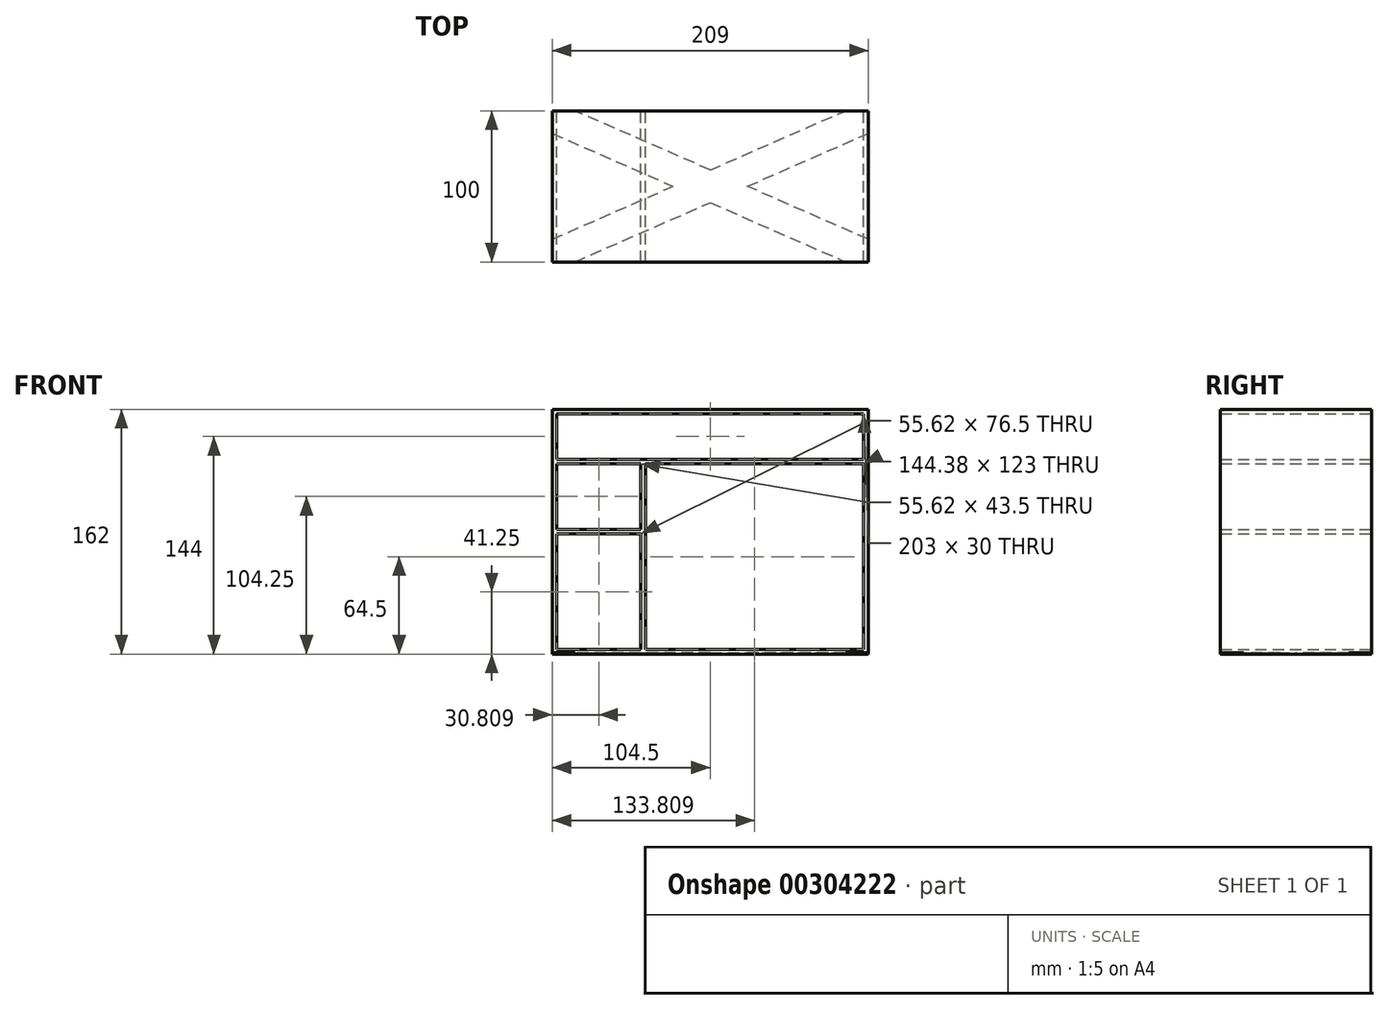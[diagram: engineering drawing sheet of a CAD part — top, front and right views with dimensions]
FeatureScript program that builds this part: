
annotation { "Feature Type Name" : "Feature", "Feature Type Description" : "" }
export const myFeature = defineFeature(function(context is Context, id is Id, definition is map)
    precondition{}
    {
        {
            var Q0;
            Q0=qCreatedBy(makeId("Front.planeOp"),FACE);
            var sketch = newSketch(context, id + "F0", { "sketchPlane" : qUnion([Q0])});
            skLineSegment(sketch, "E0.bottom", {"start": v(0, 0) * mm, "end": v(209, 0) * mm});
            skLineSegment(sketch, "E0.top", {"start": v(0, 162) * mm, "end": v(209, 162) * mm});
            skLineSegment(sketch, "E0.left", {"start": v(0, 0) * mm, "end": v(0, 162) * mm});
            skLineSegment(sketch, "E0.right", {"start": v(209, 0) * mm, "end": v(209, 162) * mm});
            skLineSegment(sketch, "E1", {"start": v(3, 159) * mm, "end": v(206, 159) * mm});
            skLineSegment(sketch, "E2", {"start": v(206, 159) * mm, "end": v(206, 129) * mm});
            skLineSegment(sketch, "E3", {"start": v(206, 3) * mm, "end": v(106, 3) * mm});
            skLineSegment(sketch, "E4", {"start": v(3, 159) * mm, "end": v(3, 129) * mm});
            skLineSegment(sketch, "E5", {"start": v(3, 129) * mm, "end": v(206, 129) * mm});
            skLineSegment(sketch, "E6", {"start": v(3, 126) * mm, "end": v(103, 126) * mm});
            skPoint(sketch, "E7.end.orphan", {"position": v(104.5, 3) * mm});
            skLineSegment(sketch, "E8", {"start": v(3, 79.5) * mm, "end": v(58.62, 79.5) * mm});
            skLineSegment(sketch, "E9", {"start": v(3, 82.5) * mm, "end": v(58.62, 82.5) * mm});
            skPoint(sketch, "E10.start.orphan", {"position": v(3, 81) * mm});
            skLineSegment(sketch, "E11.trimOffspring", {"start": v(103, 3) * mm, "end": v(3, 3) * mm});
            skLineSegment(sketch, "E12.trimOffspring", {"start": v(106, 126) * mm, "end": v(206, 126) * mm});
            skPoint(sketch, "E13.orphan", {"position": v(104.5, 126) * mm});
            skLineSegment(sketch, "E14.trimOffspring", {"start": v(206, 126) * mm, "end": v(206, 3) * mm});
            skLineSegment(sketch, "E15.trimOffspring", {"start": v(3, 126) * mm, "end": v(3, 82.5) * mm});
            skLineSegment(sketch, "E16.trimOffspring", {"start": v(3, 79.5) * mm, "end": v(3, 3) * mm});
            skLineSegment(sketch, "E17.left", {"start": v(0, 162) * mm, "end": v(0, 0) * mm});
            skLineSegment(sketch, "E17.right", {"start": v(209, 162) * mm, "end": v(209, 0) * mm});
            skLineSegment(sketch, "E18", {"start": v(58.62, 126) * mm, "end": v(58.62, 82.5) * mm});
            skLineSegment(sketch, "E19", {"start": v(61.62, 126) * mm, "end": v(61.62, 3) * mm});
            skLineSegment(sketch, "E20", {"start": v(58.62, 126) * mm, "end": v(60.12, 126) * mm, "construction": true});
            skLineSegment(sketch, "E21", {"start": v(60.12, 126) * mm, "end": v(61.62, 126) * mm, "construction": true});
            skLineSegment(sketch, "E22.trimOffspring", {"start": v(58.62, 79.5) * mm, "end": v(58.62, 3) * mm});
            skLineSegment(sketch, "E23", {"start": v(103, 126) * mm, "end": v(106, 126) * mm});
            skLineSegment(sketch, "E24", {"start": v(103, 3) * mm, "end": v(106, 3) * mm});
            skSolve(sketch);
        }
        {
            var Q0;
            Q0=makeQuery(id+"F0.imprint","IMPRINT",FACE,{"disambiguationData":[TD([[makeQuery(id+"F0.imprint","IMPRINT",EDGE,{"derivedFrom":sQuery(id+"F0.wireOp",EDGE,"E1")}),1.0]])]});
            extrude(context, id + "F1", {"entities" : qUnion([Q0]), "depth" : 100 * mm});
        }
        {
            var Q0;
            Q0=makeQuery(id+"F1.opExtrude","SWEPT_FACE",FACE,{"disambiguationData":[OSD([sQuery(id+"F0.wireOp",EDGE,"E0.bottom")])]});
            var sketch = newSketch(context, id + "F2", { "sketchPlane" : qUnion([Q0])});
            skLineSegment(sketch, "E25", {"start": v(15, 100) * mm, "end": v(104.5, 60.79) * mm});
            skLineSegment(sketch, "E26", {"start": v(0, 85) * mm, "end": v(79.88, 50) * mm});
            skLineSegment(sketch, "E27", {"start": v(0, 100) * mm, "end": v(15, 100) * mm, "construction": true});
            skLineSegment(sketch, "E28", {"start": v(0, 100) * mm, "end": v(0, 85) * mm, "construction": true});
            skLineSegment(sketch, "E29", {"start": v(209, 15) * mm, "end": v(209, 0) * mm, "construction": true});
            skLineSegment(sketch, "E30", {"start": v(209, 0) * mm, "end": v(194, 0) * mm, "construction": true});
            skLineSegment(sketch, "E31", {"start": v(0, 15) * mm, "end": v(79.88, 50) * mm});
            skLineSegment(sketch, "E32", {"start": v(209, 85) * mm, "end": v(129.12, 50) * mm});
            skLineSegment(sketch, "E33", {"start": v(0, 15) * mm, "end": v(0, 0) * mm, "construction": true});
            skLineSegment(sketch, "E34", {"start": v(0, 0) * mm, "end": v(15, 0) * mm, "construction": true});
            skLineSegment(sketch, "E35", {"start": v(194, 100) * mm, "end": v(209, 100) * mm, "construction": true});
            skLineSegment(sketch, "E36", {"start": v(209, 100) * mm, "end": v(209, 85) * mm, "construction": true});
            skLineSegment(sketch, "E37.trimOffspring", {"start": v(104.5, 60.79) * mm, "end": v(194, 100) * mm});
            skLineSegment(sketch, "E38.trimOffspring", {"start": v(104.5, 39.21) * mm, "end": v(194, 0) * mm});
            skLineSegment(sketch, "E39.trimOffspring", {"start": v(104.5, 39.21) * mm, "end": v(15, 0) * mm});
            skLineSegment(sketch, "E40.trimOffspring", {"start": v(129.12, 50) * mm, "end": v(209, 15) * mm});
            skSolve(sketch);
        }
        {
            var Q0;
            {var subQ12=sQuery(id+"F2.wireOp",EDGE,"E25");Q0=makeQuery(id+"F2.imprint","IMPRINT",FACE,{"disambiguationData":[TD([[makeQuery(id+"F2.imprint","IMPRINT",EDGE,{"derivedFrom":subQ12}),-1.0]])]});}
            extrude(context, id + "F3", {"entities" : qUnion([Q0]), "operationType" : NewBodyOperationType.REMOVE, "oppositeDirection" : true, "depth" : 1 * mm});
        }
    });
